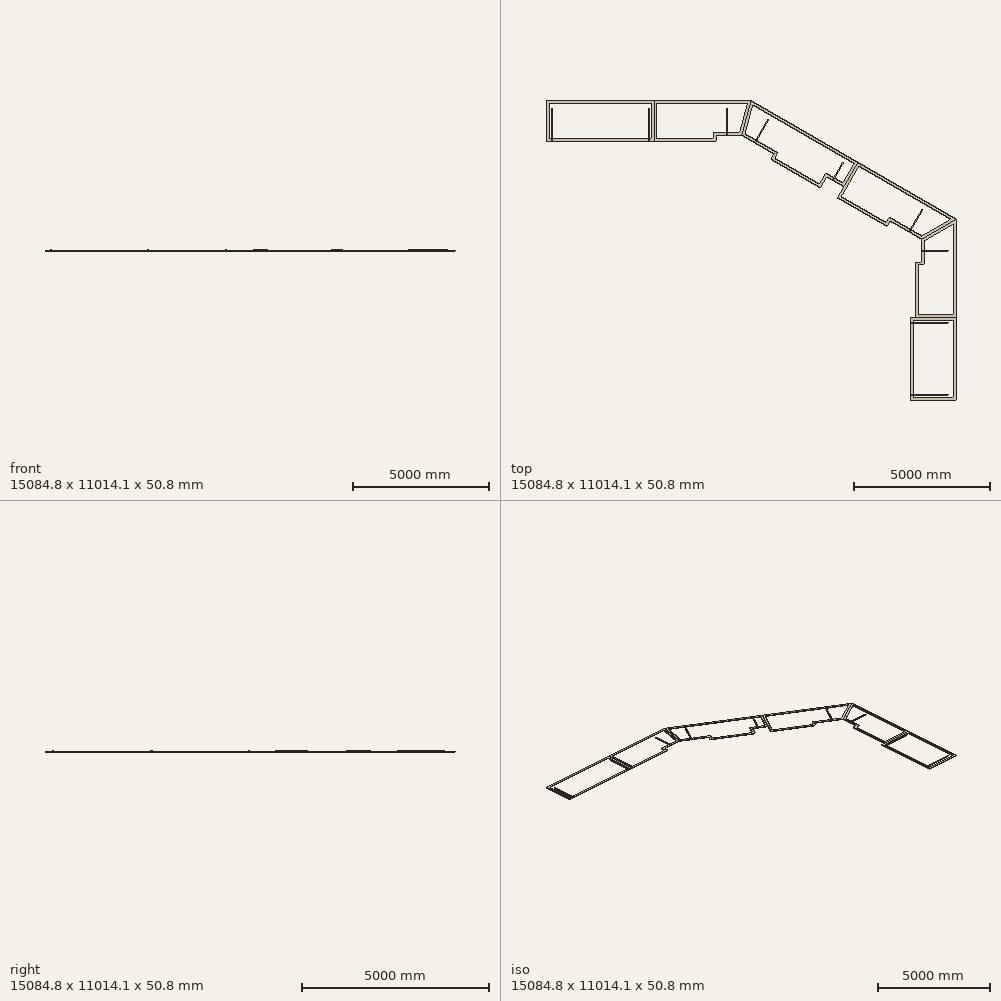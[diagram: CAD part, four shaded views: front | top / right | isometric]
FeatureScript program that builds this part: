
annotation { "Feature Type Name" : "Feature", "Feature Type Description" : "" }
export const myFeature = defineFeature(function(context is Context, id is Id, definition is map)
    precondition{}
    {
        {
            var Q0;
            Q0=qCreatedBy(makeId("Top.planeOp"),FACE);
            var sketch = newSketch(context, id + "F0", { "sketchPlane" : qUnion([Q0])});
            skLineSegment(sketch, "E0", {"start": v(0, 0) * mm, "end": v(7528.5, 0) * mm});
            skLineSegment(sketch, "E1", {"start": v(7528.5, 0) * mm, "end": v(15084.8, -4362.64) * mm});
            skLineSegment(sketch, "E2", {"start": v(15084.8, -4362.64) * mm, "end": v(15084.8, -11014.07) * mm});
            skLineSegment(sketch, "E3", {"start": v(15084.8, -11014.07) * mm, "end": v(13383, -11014.07) * mm});
            skLineSegment(sketch, "E4", {"start": v(13383, -11014.07) * mm, "end": v(13383, -7966.07) * mm});
            skLineSegment(sketch, "E5", {"start": v(13383, -7966.07) * mm, "end": v(13586.2, -7966.07) * mm});
            skLineSegment(sketch, "E6", {"start": v(13586.2, -7966.07) * mm, "end": v(13586.2, -5934.07) * mm});
            skLineSegment(sketch, "E7", {"start": v(13586.2, -5934.07) * mm, "end": v(13814.8, -5934.07) * mm});
            skLineSegment(sketch, "E8", {"start": v(13814.8, -5934.07) * mm, "end": v(13814.8, -5095.87) * mm});
            skLineSegment(sketch, "E9", {"start": v(13814.8, -5095.87) * mm, "end": v(12654.47, -4425.95) * mm});
            skLineSegment(sketch, "E10", {"start": v(12654.47, -4425.95) * mm, "end": v(12540.17, -4623.92) * mm});
            skLineSegment(sketch, "E11", {"start": v(12540.17, -4623.92) * mm, "end": v(10714.41, -3569.82) * mm});
            skLineSegment(sketch, "E12", {"start": v(10714.41, -3569.82) * mm, "end": v(10949.36, -3162.88) * mm});
            skLineSegment(sketch, "E13", {"start": v(10949.36, -3162.88) * mm, "end": v(10322.45, -2800.93) * mm});
            skLineSegment(sketch, "E14", {"start": v(10322.45, -2800.93) * mm, "end": v(10087.5, -3207.87) * mm});
            skLineSegment(sketch, "E15", {"start": v(10087.5, -3207.87) * mm, "end": v(8261.74, -2153.77) * mm});
            skLineSegment(sketch, "E16", {"start": v(8261.74, -2153.77) * mm, "end": v(8376.04, -1955.8) * mm});
            skLineSegment(sketch, "E17", {"start": v(8376.04, -1955.8) * mm, "end": v(7188.2, -1270) * mm});
            skLineSegment(sketch, "E18", {"start": v(7188.2, -1270) * mm, "end": v(6248.4, -1270) * mm});
            skLineSegment(sketch, "E19", {"start": v(6248.4, -1270) * mm, "end": v(6248.4, -1498.6) * mm});
            skLineSegment(sketch, "E20", {"start": v(6248.4, -1498.6) * mm, "end": v(0, -1498.6) * mm});
            skLineSegment(sketch, "E21", {"start": v(0, -1498.6) * mm, "end": v(0, 0) * mm});
            skLineSegment(sketch, "E22", {"start": v(3962.4, 0) * mm, "end": v(3962.4, -1498.6) * mm});
            skLineSegment(sketch, "E23", {"start": v(10949.36, -3162.88) * mm, "end": v(11463.71, -2272) * mm});
            skLineSegment(sketch, "E24", {"start": v(13586.2, -7966.07) * mm, "end": v(15084.8, -7966.07) * mm});
            skLineSegment(sketch, "E25", {"start": v(7188.2, -1270) * mm, "end": v(7528.5, 0) * mm});
            skLineSegment(sketch, "E26", {"start": v(13814.8, -5095.87) * mm, "end": v(15084.8, -4362.64) * mm});
            skLineSegment(sketch, "E27.0", {"start": v(6146.8, -1397) * mm, "end": v(4064, -1397) * mm});
            skLineSegment(sketch, "E27.1", {"start": v(6146.8, -1168.4) * mm, "end": v(6146.8, -1397) * mm});
            skLineSegment(sketch, "E27.2", {"start": v(7110.24, -1168.4) * mm, "end": v(6146.8, -1168.4) * mm});
            skLineSegment(sketch, "E27.3", {"start": v(8514.83, -1918.61) * mm, "end": v(7306.52, -1221) * mm});
            skLineSegment(sketch, "E27.4", {"start": v(8400.53, -2116.59) * mm, "end": v(8514.83, -1918.61) * mm});
            skLineSegment(sketch, "E27.5", {"start": v(101.6, -1397) * mm, "end": v(101.6, -101.6) * mm});
            skLineSegment(sketch, "E27.6", {"start": v(10050.3, -3069.09) * mm, "end": v(8400.53, -2116.59) * mm});
            skLineSegment(sketch, "E27.7", {"start": v(10285.26, -2662.14) * mm, "end": v(10050.3, -3069.09) * mm});
            skLineSegment(sketch, "E27.9", {"start": v(10853.2, -3532.64) * mm, "end": v(11045.25, -3200) * mm});
            skLineSegment(sketch, "E27.10", {"start": v(12502.98, -4485.14) * mm, "end": v(10853.2, -3532.64) * mm});
            skLineSegment(sketch, "E27.11", {"start": v(12617.28, -4287.16) * mm, "end": v(12502.98, -4485.14) * mm});
            skLineSegment(sketch, "E27.12", {"start": v(14983.2, -10912.47) * mm, "end": v(13484.6, -10912.47) * mm});
            skLineSegment(sketch, "E27.13", {"start": v(14983.2, -4538.62) * mm, "end": v(14983.2, -7864.47) * mm});
            skLineSegment(sketch, "E27.14", {"start": v(7501.27, -101.6) * mm, "end": v(7501.27, -101.6) * mm});
            skLineSegment(sketch, "E27.15", {"start": v(101.6, -101.6) * mm, "end": v(3860.8, -101.6) * mm});
            skLineSegment(sketch, "E27.16", {"start": v(13484.6, -10912.47) * mm, "end": v(13484.6, -8067.67) * mm});
            skLineSegment(sketch, "E27.17", {"start": v(13484.6, -8067.67) * mm, "end": v(13531.47, -8067.67) * mm});
            skLineSegment(sketch, "E27.19", {"start": v(13687.8, -6035.67) * mm, "end": v(13916.4, -6035.67) * mm});
            skLineSegment(sketch, "E27.20", {"start": v(13916.4, -6035.67) * mm, "end": v(13916.4, -5154.53) * mm});
            skLineSegment(sketch, "E27.21", {"start": v(13814.8, -4978.56) * mm, "end": v(12617.28, -4287.16) * mm});
            skLineSegment(sketch, "E28.0", {"start": v(3860.8, -101.6) * mm, "end": v(3860.8, -1397) * mm});
            skLineSegment(sketch, "E29.0", {"start": v(4064, -101.6) * mm, "end": v(4064, -1397) * mm});
            skLineSegment(sketch, "E30.0", {"start": v(7306.52, -1221) * mm, "end": v(7592.36, -154.2) * mm});
            skLineSegment(sketch, "E31.0", {"start": v(7110.24, -1168.4) * mm, "end": v(7396.09, -101.6) * mm});
            skLineSegment(sketch, "E32.trimOffspring", {"start": v(4064, -101.6) * mm, "end": v(7396.09, -101.6) * mm});
            skLineSegment(sketch, "E33.trimOffspring", {"start": v(3860.8, -1397) * mm, "end": v(101.6, -1397) * mm});
            skLineSegment(sketch, "E34.trimOffspring", {"start": v(7592.36, -154.2) * mm, "end": v(11324.92, -2309.19) * mm});
            skLineSegment(sketch, "E35.trimOffspring", {"start": v(7215.42, -1168.4) * mm, "end": v(7215.42, -1168.4) * mm});
            skLineSegment(sketch, "E36.0", {"start": v(10994.45, -3287.99) * mm, "end": v(11500.9, -2410.79) * mm});
            skLineSegment(sketch, "E37.0", {"start": v(10912.17, -3024.09) * mm, "end": v(11324.92, -2309.19) * mm});
            skLineSegment(sketch, "E38.0", {"start": v(13916.4, -5154.53) * mm, "end": v(14983.2, -4538.62) * mm});
            skLineSegment(sketch, "E39.0", {"start": v(13814.8, -4978.56) * mm, "end": v(14881.6, -4362.64) * mm});
            skLineSegment(sketch, "E40.0", {"start": v(13429.87, -8067.67) * mm, "end": v(14983.2, -8067.67) * mm});
            skLineSegment(sketch, "E41.0", {"start": v(13687.8, -7864.47) * mm, "end": v(14983.2, -7864.47) * mm});
            skLineSegment(sketch, "E42.trimOffspring", {"start": v(10912.17, -3024.09) * mm, "end": v(10285.26, -2662.14) * mm});
            skLineSegment(sketch, "E43.trimOffspring", {"start": v(11500.9, -2410.79) * mm, "end": v(14881.6, -4362.64) * mm});
            skLineSegment(sketch, "E44.trimOffspring", {"start": v(11514.98, -2386.39) * mm, "end": v(11551.7, -2322.8) * mm});
            skLineSegment(sketch, "E45.trimOffspring", {"start": v(13916.4, -5037.22) * mm, "end": v(13916.4, -5037.22) * mm});
            skLineSegment(sketch, "E46.trimOffspring", {"start": v(14983.2, -4421.3) * mm, "end": v(14983.2, -4421.3) * mm});
            skLineSegment(sketch, "E47.trimOffspring", {"start": v(13687.8, -7864.47) * mm, "end": v(13687.8, -6035.67) * mm});
            skLineSegment(sketch, "E48.trimOffspring", {"start": v(14983.2, -8067.67) * mm, "end": v(14983.2, -10912.47) * mm});
            skLineSegment(sketch, "E49", {"start": v(15084.8, -4362.64) * mm, "end": v(14983.2, -4538.62) * mm});
            skSolve(sketch);
        }
        {
            var Q0;
            {var subQ1=sQuery(id+"F0.wireOp",EDGE,"E21");Q0=makeQuery(id+"F0.imprint","IMPRINT",FACE,{"disambiguationData":[TD([[makeQuery(id+"F0.imprint","IMPRINT",EDGE,{"derivedFrom":subQ1}),-1.0]])]});}
            extrude(context, id + "F1", {"entities" : qUnion([Q0]), "depth" : 25.4 * mm, "offsetDistance" : 25.4 * mm});
        }
        {
            var Q0;
            {var subQ5=sQuery(id+"F0.wireOp",EDGE,"E18");Q0=makeQuery(id+"F0.imprint","IMPRINT",FACE,{"disambiguationData":[TD([[makeQuery(id+"F0.imprint","IMPRINT",EDGE,{"derivedFrom":subQ5}),-1.0]])]});}
            extrude(context, id + "F2", {"entities" : qUnion([Q0]), "depth" : 25.4 * mm, "offsetDistance" : 25.4 * mm});
        }
        {
            var Q0;
            Q0=makeQuery(id+"F0.imprint","IMPRINT",FACE,{"disambiguationData":[TD([[makeQuery(id+"F0.imprint","IMPRINT",EDGE,{"derivedFrom":sQuery(id+"F0.wireOp",EDGE,"E13")}),-1.0]])]});
            extrude(context, id + "F3", {"entities" : qUnion([Q0]), "depth" : 25.4 * mm, "offsetDistance" : 25.4 * mm});
        }
        {
            var Q0;
            {var subQ3=sQuery(id+"F0.wireOp",EDGE,"E9");Q0=makeQuery(id+"F0.imprint","IMPRINT",FACE,{"disambiguationData":[TD([[makeQuery(id+"F0.imprint","IMPRINT",EDGE,{"derivedFrom":subQ3}),-1.0]])]});}
            extrude(context, id + "F4", {"entities" : qUnion([Q0]), "depth" : 25.4 * mm, "offsetDistance" : 25.4 * mm});
        }
        {
            var Q0;
            Q0=makeQuery(id+"F0.imprint","IMPRINT",FACE,{"disambiguationData":[TD([[makeQuery(id+"F0.imprint","IMPRINT",EDGE,{"derivedFrom":sQuery(id+"F0.wireOp",EDGE,"E6")}),-1.0]])]});
            extrude(context, id + "F5", {"entities" : qUnion([Q0]), "depth" : 25.4 * mm, "offsetDistance" : 25.4 * mm});
        }
        {
            var Q0;
            {var subQ4=sQuery(id+"F0.wireOp",EDGE,"E3");Q0=makeQuery(id+"F0.imprint","IMPRINT",FACE,{"disambiguationData":[TD([[makeQuery(id+"F0.imprint","IMPRINT",EDGE,{"derivedFrom":subQ4}),-1.0]])]});}
            extrude(context, id + "F6", {"entities" : qUnion([Q0]), "depth" : 25.4 * mm, "offsetDistance" : 25.4 * mm});
        }
        {
            var Q0;
            Q0=makeQuery(id+"F1.opExtrude","CAP_FACE",FACE,{"disambiguationData":[OSD([sQuery(id+"F0.wireOp",EDGE,"E0"),sQuery(id+"F0.wireOp",EDGE,"E20"),sQuery(id+"F0.wireOp",EDGE,"E21"),sQuery(id+"F0.wireOp",EDGE,"E22"),sQuery(id+"F0.wireOp",EDGE,"E27.5"),sQuery(id+"F0.wireOp",EDGE,"E27.15"),sQuery(id+"F0.wireOp",EDGE,"E28.0"),sQuery(id+"F0.wireOp",EDGE,"E33.trimOffspring")])],"isStart":false});
            var sketch = newSketch(context, id + "F7", { "sketchPlane" : qUnion([Q0])});
            skLineSegment(sketch, "E50.bottom", {"start": v(184.15, -1498.6) * mm, "end": v(222.25, -1498.6) * mm});
            skLineSegment(sketch, "E50.top", {"start": v(184.15, -304.8) * mm, "end": v(222.25, -304.8) * mm});
            skLineSegment(sketch, "E50.left", {"start": v(184.15, -1498.6) * mm, "end": v(184.15, -304.8) * mm});
            skLineSegment(sketch, "E50.right", {"start": v(222.25, -1498.6) * mm, "end": v(222.25, -304.8) * mm});
            skLineSegment(sketch, "E51.bottom", {"start": v(3752.85, -1498.6) * mm, "end": v(3790.95, -1498.6) * mm});
            skLineSegment(sketch, "E51.top", {"start": v(3752.85, -304.8) * mm, "end": v(3790.95, -304.8) * mm});
            skLineSegment(sketch, "E51.left", {"start": v(3752.85, -1498.6) * mm, "end": v(3752.85, -304.8) * mm});
            skLineSegment(sketch, "E51.right", {"start": v(3790.95, -1498.6) * mm, "end": v(3790.95, -304.8) * mm});
            skLineSegment(sketch, "E52.bottom", {"start": v(6623.05, -1270) * mm, "end": v(6661.15, -1270) * mm});
            skLineSegment(sketch, "E52.top", {"start": v(6623.05, -304.8) * mm, "end": v(6661.15, -304.8) * mm});
            skLineSegment(sketch, "E52.left", {"start": v(6623.05, -1270) * mm, "end": v(6623.05, -304.8) * mm});
            skLineSegment(sketch, "E52.right", {"start": v(6661.15, -1270) * mm, "end": v(6661.15, -304.8) * mm});
            skCircle(sketch, "E53", {"center": v(203.2, -304.8) * mm, "radius": 19.05 * mm});
            skCircle(sketch, "E54", {"center": v(3771.9, -304.8) * mm, "radius": 19.05 * mm});
            skCircle(sketch, "E55", {"center": v(6642.1, -304.8) * mm, "radius": 19.05 * mm});
            skLineSegment(sketch, "E56", {"start": v(7655.64, -1539.88) * mm, "end": v(8138.24, -703.99) * mm});
            skLineSegment(sketch, "E57", {"start": v(8138.24, -703.99) * mm, "end": v(8171.23, -723.04) * mm});
            skLineSegment(sketch, "E58", {"start": v(8171.23, -723.04) * mm, "end": v(7688.63, -1558.93) * mm});
            skLineSegment(sketch, "E59", {"start": v(7688.63, -1558.92) * mm, "end": v(7655.64, -1539.88) * mm});
            skCircle(sketch, "E60", {"center": v(8154.73, -713.51) * mm, "radius": 19.05 * mm});
            skLineSegment(sketch, "E61", {"start": v(10887.87, -2291.49) * mm, "end": v(10525.92, -2918.4) * mm});
            skLineSegment(sketch, "E62", {"start": v(10525.92, -2918.4) * mm, "end": v(10558.91, -2937.45) * mm});
            skLineSegment(sketch, "E63", {"start": v(10558.91, -2937.45) * mm, "end": v(10920.86, -2310.54) * mm});
            skLineSegment(sketch, "E64", {"start": v(10920.86, -2310.54) * mm, "end": v(10887.87, -2291.49) * mm});
            skCircle(sketch, "E65", {"center": v(10904.37, -2301.01) * mm, "radius": 19.05 * mm});
            skLineSegment(sketch, "E66", {"start": v(13824.47, -3986.94) * mm, "end": v(13341.87, -4822.82) * mm});
            skLineSegment(sketch, "E67", {"start": v(13341.87, -4822.82) * mm, "end": v(13374.87, -4841.87) * mm});
            skLineSegment(sketch, "E68", {"start": v(13374.87, -4841.87) * mm, "end": v(13857.47, -4005.99) * mm});
            skLineSegment(sketch, "E69", {"start": v(13857.47, -4005.99) * mm, "end": v(13824.47, -3986.94) * mm});
            skCircle(sketch, "E70", {"center": v(13840.97, -3996.46) * mm, "radius": 19.05 * mm});
            skLineSegment(sketch, "E71.bottom", {"start": v(13814.8, -5521.32) * mm, "end": v(14780, -5521.32) * mm});
            skLineSegment(sketch, "E71.top", {"start": v(13814.8, -5559.42) * mm, "end": v(14780, -5559.42) * mm});
            skLineSegment(sketch, "E71.left", {"start": v(13814.8, -5521.32) * mm, "end": v(13814.8, -5559.42) * mm});
            skLineSegment(sketch, "E71.right", {"start": v(14780, -5521.32) * mm, "end": v(14780, -5559.42) * mm});
            skLineSegment(sketch, "E72.bottom", {"start": v(13383, -8150.22) * mm, "end": v(14780, -8150.22) * mm});
            skLineSegment(sketch, "E72.top", {"start": v(13383, -8188.32) * mm, "end": v(14780, -8188.32) * mm});
            skLineSegment(sketch, "E72.left", {"start": v(13383, -8150.22) * mm, "end": v(13383, -8188.32) * mm});
            skLineSegment(sketch, "E72.right", {"start": v(14780, -8150.22) * mm, "end": v(14780, -8188.32) * mm});
            skLineSegment(sketch, "E73.bottom", {"start": v(13383, -10791.82) * mm, "end": v(14780, -10791.82) * mm});
            skLineSegment(sketch, "E73.top", {"start": v(13383, -10829.92) * mm, "end": v(14780, -10829.92) * mm});
            skLineSegment(sketch, "E73.left", {"start": v(13383, -10791.82) * mm, "end": v(13383, -10829.92) * mm});
            skLineSegment(sketch, "E73.right", {"start": v(14780, -10791.82) * mm, "end": v(14780, -10829.92) * mm});
            skCircle(sketch, "E74", {"center": v(14780, -10810.87) * mm, "radius": 19.05 * mm});
            skCircle(sketch, "E75", {"center": v(14780, -8169.27) * mm, "radius": 19.05 * mm});
            skCircle(sketch, "E76", {"center": v(14780, -5540.37) * mm, "radius": 19.05 * mm});
            skSolve(sketch);
        }
        {
            var Q0;
            Q0 = qSketchRegion(id + "F7", true);
            extrude(context, id + "F8", {"entities" : qUnion([Q0]), "depth" : 25.4 * mm, "offsetDistance" : 25.4 * mm});
        }
    });
